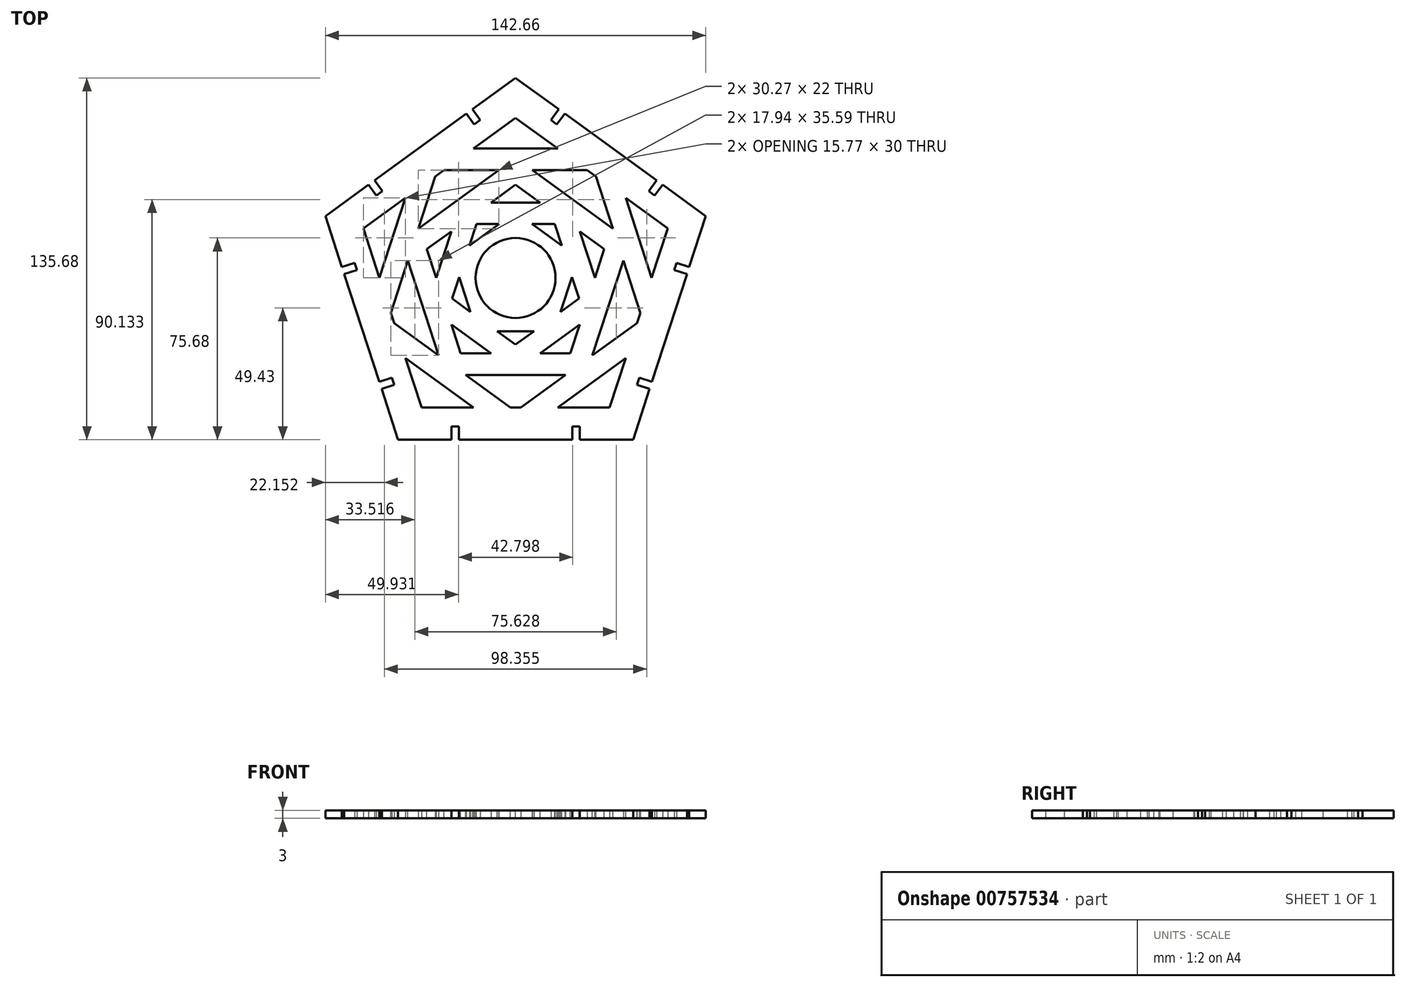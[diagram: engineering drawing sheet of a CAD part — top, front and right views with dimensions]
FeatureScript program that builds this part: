
annotation { "Feature Type Name" : "Feature", "Feature Type Description" : "" }
export const myFeature = defineFeature(function(context is Context, id is Id, definition is map)
    precondition{}
    {
        {
            var Q0;
            Q0=qCreatedBy(makeId("Top.planeOp"),FACE);
            var sketch = newSketch(context, id + "F0", { "sketchPlane" : qUnion([Q0])});
            skCircle(sketch, "E0.cCircle", {"center": v(0, 0) * mm, "radius": 75 * mm, "construction": true});
            skLineSegment(sketch, "E0.0", {"start": v(0, 75) * mm, "end": v(16.18, 63.24) * mm});
            skLineSegment(sketch, "E0.1", {"start": v(71.33, 23.18) * mm, "end": v(65.15, 4.16) * mm});
            skLineSegment(sketch, "E0.2", {"start": v(44.08, -60.68) * mm, "end": v(24.08, -60.68) * mm});
            skLineSegment(sketch, "E0.3", {"start": v(-44.08, -60.68) * mm, "end": v(-50.26, -41.66) * mm});
            skLineSegment(sketch, "E0.4", {"start": v(-71.33, 23.18) * mm, "end": v(-55.15, 34.93) * mm});
            skLineSegment(sketch, "E1", {"start": v(-16.18, 63.24) * mm, "end": v(-13.24, 59.2) * mm});
            skLineSegment(sketch, "E2", {"start": v(-13.24, 59.2) * mm, "end": v(-15.5, 57.55) * mm});
            skLineSegment(sketch, "E3", {"start": v(-15.5, 57.55) * mm, "end": v(-18.45, 61.6) * mm});
            skLineSegment(sketch, "E4", {"start": v(-35.66, 49.09) * mm, "end": v(44.08, -60.68) * mm, "construction": true});
            skLineSegment(sketch, "E5", {"start": v(-44.08, -60.68) * mm, "end": v(35.66, 49.09) * mm, "construction": true});
            skLineSegment(sketch, "E6", {"start": v(-71.33, 23.18) * mm, "end": v(57.7, -18.75) * mm, "construction": true});
            skLineSegment(sketch, "E7", {"start": v(71.33, 23.18) * mm, "end": v(-57.7, -18.75) * mm, "construction": true});
            skLineSegment(sketch, "E8", {"start": v(0, 75) * mm, "end": v(0, -60.68) * mm, "construction": true});
            skLineSegment(sketch, "E9.trimOffspring", {"start": v(-16.18, 63.24) * mm, "end": v(0, 75) * mm});
            skLineSegment(sketch, "E10.MirrorCS", {"start": v(-55.15, 34.93) * mm, "end": v(-52.2, 30.89) * mm});
            skLineSegment(sketch, "E11.MirrorCS", {"start": v(-49.94, 32.53) * mm, "end": v(-52.88, 36.58) * mm});
            skLineSegment(sketch, "E12.MirrorCS", {"start": v(-52.2, 30.89) * mm, "end": v(-49.94, 32.53) * mm});
            skLineSegment(sketch, "E13.trimOffspring", {"start": v(-52.88, 36.58) * mm, "end": v(-18.45, 61.6) * mm});
            skLineSegment(sketch, "E14.1.0", {"start": v(-65.15, 4.16) * mm, "end": v(-60.4, 5.7) * mm});
            skLineSegment(sketch, "E14.1.1", {"start": v(-59.53, 3.04) * mm, "end": v(-64.28, 1.5) * mm});
            skLineSegment(sketch, "E14.1.2", {"start": v(-60.4, 5.7) * mm, "end": v(-59.53, 3.04) * mm});
            skLineSegment(sketch, "E14.1.3", {"start": v(-46.37, -37.45) * mm, "end": v(-51.13, -39) * mm});
            skLineSegment(sketch, "E14.1.4", {"start": v(-45.5, -40.11) * mm, "end": v(-46.37, -37.45) * mm});
            skLineSegment(sketch, "E14.1.5", {"start": v(-50.26, -41.66) * mm, "end": v(-45.5, -40.11) * mm});
            skLineSegment(sketch, "E14.2.0", {"start": v(-24.08, -60.68) * mm, "end": v(-24.08, -55.68) * mm});
            skLineSegment(sketch, "E14.2.1", {"start": v(-21.28, -55.68) * mm, "end": v(-21.28, -60.68) * mm});
            skLineSegment(sketch, "E14.2.2", {"start": v(-24.08, -55.68) * mm, "end": v(-21.28, -55.68) * mm});
            skLineSegment(sketch, "E14.2.3", {"start": v(21.28, -55.68) * mm, "end": v(21.28, -60.68) * mm});
            skLineSegment(sketch, "E14.2.4", {"start": v(24.08, -55.68) * mm, "end": v(21.28, -55.68) * mm});
            skLineSegment(sketch, "E14.2.5", {"start": v(24.08, -60.68) * mm, "end": v(24.08, -55.68) * mm});
            skLineSegment(sketch, "E14.3.0", {"start": v(50.26, -41.66) * mm, "end": v(45.5, -40.11) * mm});
            skLineSegment(sketch, "E14.3.1", {"start": v(46.37, -37.45) * mm, "end": v(51.13, -39) * mm});
            skLineSegment(sketch, "E14.3.2", {"start": v(45.5, -40.11) * mm, "end": v(46.37, -37.45) * mm});
            skLineSegment(sketch, "E14.3.3", {"start": v(59.53, 3.04) * mm, "end": v(64.28, 1.5) * mm});
            skLineSegment(sketch, "E14.3.4", {"start": v(60.4, 5.7) * mm, "end": v(59.53, 3.04) * mm});
            skLineSegment(sketch, "E14.3.5", {"start": v(65.15, 4.16) * mm, "end": v(60.4, 5.7) * mm});
            skLineSegment(sketch, "E14.4.0", {"start": v(55.15, 34.93) * mm, "end": v(52.2, 30.89) * mm});
            skLineSegment(sketch, "E14.4.1", {"start": v(49.94, 32.53) * mm, "end": v(52.88, 36.58) * mm});
            skLineSegment(sketch, "E14.4.2", {"start": v(52.2, 30.89) * mm, "end": v(49.94, 32.53) * mm});
            skLineSegment(sketch, "E14.4.3", {"start": v(15.5, 57.55) * mm, "end": v(18.45, 61.6) * mm});
            skLineSegment(sketch, "E14.4.4", {"start": v(13.24, 59.2) * mm, "end": v(15.5, 57.55) * mm});
            skLineSegment(sketch, "E14.4.5", {"start": v(16.18, 63.24) * mm, "end": v(13.24, 59.2) * mm});
            skLineSegment(sketch, "E15.trimOffspring", {"start": v(-65.15, 4.16) * mm, "end": v(-71.33, 23.18) * mm});
            skLineSegment(sketch, "E16.trimOffspring", {"start": v(21.28, -60.68) * mm, "end": v(-21.28, -60.68) * mm});
            skLineSegment(sketch, "E17.trimOffspring", {"start": v(-24.08, -60.68) * mm, "end": v(-44.08, -60.68) * mm});
            skLineSegment(sketch, "E18.trimOffspring", {"start": v(-51.13, -39) * mm, "end": v(-64.28, 1.5) * mm});
            skLineSegment(sketch, "E19.trimOffspring", {"start": v(18.45, 61.6) * mm, "end": v(52.88, 36.58) * mm});
            skLineSegment(sketch, "E20.trimOffspring", {"start": v(55.15, 34.93) * mm, "end": v(71.33, 23.18) * mm});
            skLineSegment(sketch, "E21.trimOffspring", {"start": v(64.28, 1.5) * mm, "end": v(51.13, -39) * mm});
            skLineSegment(sketch, "E22.trimOffspring", {"start": v(50.26, -41.66) * mm, "end": v(44.08, -60.68) * mm});
            skCircle(sketch, "E23.cCircle", {"center": v(0, 0) * mm, "radius": 60 * mm, "construction": true});
            skLineSegment(sketch, "E23.0", {"start": v(0, 60) * mm, "end": v(57.06, 18.54) * mm});
            skLineSegment(sketch, "E23.1", {"start": v(57.06, 18.54) * mm, "end": v(35.27, -48.54) * mm});
            skLineSegment(sketch, "E23.2", {"start": v(35.27, -48.54) * mm, "end": v(-35.27, -48.54) * mm});
            skLineSegment(sketch, "E23.3", {"start": v(-35.27, -48.54) * mm, "end": v(-57.06, 18.54) * mm});
            skLineSegment(sketch, "E23.4", {"start": v(-57.06, 18.54) * mm, "end": v(0, 60) * mm});
            skSolve(sketch);
        }
        {
            var Q0;
            Q0 = qSketchRegion(id + "F0", true);
            extrude(context, id + "F1", {"entities" : qUnion([Q0]), "depth" : 3 * mm, "offsetDistance" : 25 * mm});
        }
        {
            var Q0;
            Q0=makeQuery(id+"F1.opExtrude","CAP_FACE",FACE,{"disambiguationData":[OSD([sQuery(id+"F0.wireOp",EDGE,"E0.0"),sQuery(id+"F0.wireOp",EDGE,"E0.1"),sQuery(id+"F0.wireOp",EDGE,"E0.2"),sQuery(id+"F0.wireOp",EDGE,"E0.3"),sQuery(id+"F0.wireOp",EDGE,"E0.4"),sQuery(id+"F0.wireOp",EDGE,"E1"),sQuery(id+"F0.wireOp",EDGE,"E2"),sQuery(id+"F0.wireOp",EDGE,"E3"),sQuery(id+"F0.wireOp",EDGE,"E9.trimOffspring"),sQuery(id+"F0.wireOp",EDGE,"E10.MirrorCS"),sQuery(id+"F0.wireOp",EDGE,"E11.MirrorCS"),sQuery(id+"F0.wireOp",EDGE,"E12.MirrorCS"),sQuery(id+"F0.wireOp",EDGE,"E13.trimOffspring"),sQuery(id+"F0.wireOp",EDGE,"E14.1.0"),sQuery(id+"F0.wireOp",EDGE,"E14.1.1"),sQuery(id+"F0.wireOp",EDGE,"E14.1.2"),sQuery(id+"F0.wireOp",EDGE,"E14.1.3"),sQuery(id+"F0.wireOp",EDGE,"E14.1.4"),sQuery(id+"F0.wireOp",EDGE,"E14.1.5"),sQuery(id+"F0.wireOp",EDGE,"E14.2.0"),sQuery(id+"F0.wireOp",EDGE,"E14.2.1"),sQuery(id+"F0.wireOp",EDGE,"E14.2.2"),sQuery(id+"F0.wireOp",EDGE,"E14.2.3"),sQuery(id+"F0.wireOp",EDGE,"E14.2.4"),sQuery(id+"F0.wireOp",EDGE,"E14.2.5"),sQuery(id+"F0.wireOp",EDGE,"E14.3.0"),sQuery(id+"F0.wireOp",EDGE,"E14.3.1"),sQuery(id+"F0.wireOp",EDGE,"E14.3.2"),sQuery(id+"F0.wireOp",EDGE,"E14.3.3"),sQuery(id+"F0.wireOp",EDGE,"E14.3.4"),sQuery(id+"F0.wireOp",EDGE,"E14.3.5"),sQuery(id+"F0.wireOp",EDGE,"E14.4.0"),sQuery(id+"F0.wireOp",EDGE,"E14.4.1"),sQuery(id+"F0.wireOp",EDGE,"E14.4.2"),sQuery(id+"F0.wireOp",EDGE,"E14.4.3"),sQuery(id+"F0.wireOp",EDGE,"E14.4.4"),sQuery(id+"F0.wireOp",EDGE,"E14.4.5"),sQuery(id+"F0.wireOp",EDGE,"E15.trimOffspring"),sQuery(id+"F0.wireOp",EDGE,"E16.trimOffspring"),sQuery(id+"F0.wireOp",EDGE,"E17.trimOffspring"),sQuery(id+"F0.wireOp",EDGE,"E18.trimOffspring"),sQuery(id+"F0.wireOp",EDGE,"E19.trimOffspring"),sQuery(id+"F0.wireOp",EDGE,"E20.trimOffspring"),sQuery(id+"F0.wireOp",EDGE,"E21.trimOffspring"),sQuery(id+"F0.wireOp",EDGE,"E22.trimOffspring"),sQuery(id+"F0.wireOp",EDGE,"E23.0"),sQuery(id+"F0.wireOp",EDGE,"E23.1"),sQuery(id+"F0.wireOp",EDGE,"E23.2"),sQuery(id+"F0.wireOp",EDGE,"E23.3"),sQuery(id+"F0.wireOp",EDGE,"E23.4")])],"isStart":false});
            var sketch = newSketch(context, id + "F2", { "sketchPlane" : qUnion([Q0])});
            skCircle(sketch, "E24.cCircle", {"center": v(0, 0) * mm, "radius": 60 * mm, "construction": true});
            skLineSegment(sketch, "E24.0", {"start": v(0, -60) * mm, "end": v(-57.06, -18.54) * mm});
            skLineSegment(sketch, "E24.1", {"start": v(-57.06, -18.54) * mm, "end": v(-35.27, 48.54) * mm});
            skLineSegment(sketch, "E24.2", {"start": v(-35.27, 48.54) * mm, "end": v(35.27, 48.54) * mm});
            skLineSegment(sketch, "E24.3", {"start": v(35.27, 48.54) * mm, "end": v(57.06, -18.54) * mm});
            skLineSegment(sketch, "E24.4", {"start": v(57.06, -18.54) * mm, "end": v(0, -60) * mm});
            skCircle(sketch, "E25.cCircle", {"center": v(0, 0) * mm, "radius": 50 * mm, "construction": true});
            skLineSegment(sketch, "E25.0", {"start": v(0, -50) * mm, "end": v(-47.55, -15.45) * mm});
            skLineSegment(sketch, "E25.1", {"start": v(-47.55, -15.45) * mm, "end": v(-29.39, 40.45) * mm});
            skLineSegment(sketch, "E25.2", {"start": v(-29.39, 40.45) * mm, "end": v(29.39, 40.45) * mm});
            skLineSegment(sketch, "E25.3", {"start": v(29.39, 40.45) * mm, "end": v(47.55, -15.45) * mm});
            skLineSegment(sketch, "E25.4", {"start": v(47.55, -15.45) * mm, "end": v(0, -50) * mm});
            skSolve(sketch);
        }
        {
            var Q0;
            Q0 = qSketchRegion(id + "F2", true);
            extrude(context, id + "F3", {"entities" : qUnion([Q0]), "operationType" : NewBodyOperationType.ADD, "oppositeDirection" : true, "depth" : 3 * mm, "offsetDistance" : 25 * mm});
        }
        {
            var Q0;
            Q0=makeQuery(id+"F3.boolean.opBoolean","MERGE",FACE,{"derivedFrom":[makeQuery(id+"F1.opExtrude","CAP_FACE",FACE,{"disambiguationData":[OSD([sQuery(id+"F0.wireOp",EDGE,"E0.0"),sQuery(id+"F0.wireOp",EDGE,"E0.1"),sQuery(id+"F0.wireOp",EDGE,"E0.2"),sQuery(id+"F0.wireOp",EDGE,"E0.3"),sQuery(id+"F0.wireOp",EDGE,"E0.4"),sQuery(id+"F0.wireOp",EDGE,"E1"),sQuery(id+"F0.wireOp",EDGE,"E2"),sQuery(id+"F0.wireOp",EDGE,"E3"),sQuery(id+"F0.wireOp",EDGE,"E9.trimOffspring"),sQuery(id+"F0.wireOp",EDGE,"E10.MirrorCS"),sQuery(id+"F0.wireOp",EDGE,"E11.MirrorCS"),sQuery(id+"F0.wireOp",EDGE,"E12.MirrorCS"),sQuery(id+"F0.wireOp",EDGE,"E13.trimOffspring"),sQuery(id+"F0.wireOp",EDGE,"E14.1.0"),sQuery(id+"F0.wireOp",EDGE,"E14.1.1"),sQuery(id+"F0.wireOp",EDGE,"E14.1.2"),sQuery(id+"F0.wireOp",EDGE,"E14.1.3"),sQuery(id+"F0.wireOp",EDGE,"E14.1.4"),sQuery(id+"F0.wireOp",EDGE,"E14.1.5"),sQuery(id+"F0.wireOp",EDGE,"E14.2.0"),sQuery(id+"F0.wireOp",EDGE,"E14.2.1"),sQuery(id+"F0.wireOp",EDGE,"E14.2.2"),sQuery(id+"F0.wireOp",EDGE,"E14.2.3"),sQuery(id+"F0.wireOp",EDGE,"E14.2.4"),sQuery(id+"F0.wireOp",EDGE,"E14.2.5"),sQuery(id+"F0.wireOp",EDGE,"E14.3.0"),sQuery(id+"F0.wireOp",EDGE,"E14.3.1"),sQuery(id+"F0.wireOp",EDGE,"E14.3.2"),sQuery(id+"F0.wireOp",EDGE,"E14.3.3"),sQuery(id+"F0.wireOp",EDGE,"E14.3.4"),sQuery(id+"F0.wireOp",EDGE,"E14.3.5"),sQuery(id+"F0.wireOp",EDGE,"E14.4.0"),sQuery(id+"F0.wireOp",EDGE,"E14.4.1"),sQuery(id+"F0.wireOp",EDGE,"E14.4.2"),sQuery(id+"F0.wireOp",EDGE,"E14.4.3"),sQuery(id+"F0.wireOp",EDGE,"E14.4.4"),sQuery(id+"F0.wireOp",EDGE,"E14.4.5"),sQuery(id+"F0.wireOp",EDGE,"E15.trimOffspring"),sQuery(id+"F0.wireOp",EDGE,"E16.trimOffspring"),sQuery(id+"F0.wireOp",EDGE,"E17.trimOffspring"),sQuery(id+"F0.wireOp",EDGE,"E18.trimOffspring"),sQuery(id+"F0.wireOp",EDGE,"E19.trimOffspring"),sQuery(id+"F0.wireOp",EDGE,"E20.trimOffspring"),sQuery(id+"F0.wireOp",EDGE,"E21.trimOffspring"),sQuery(id+"F0.wireOp",EDGE,"E22.trimOffspring"),sQuery(id+"F0.wireOp",EDGE,"E23.0"),sQuery(id+"F0.wireOp",EDGE,"E23.1"),sQuery(id+"F0.wireOp",EDGE,"E23.2"),sQuery(id+"F0.wireOp",EDGE,"E23.3"),sQuery(id+"F0.wireOp",EDGE,"E23.4")])],"isStart":false}),makeQuery(id+"F3.opExtrude","CAP_FACE",FACE,{"disambiguationData":[OSD([sQuery(id+"F2.wireOp",EDGE,"E24.0"),sQuery(id+"F2.wireOp",EDGE,"E24.1"),sQuery(id+"F2.wireOp",EDGE,"E24.2"),sQuery(id+"F2.wireOp",EDGE,"E24.3"),sQuery(id+"F2.wireOp",EDGE,"E24.4"),sQuery(id+"F2.wireOp",EDGE,"E25.0"),sQuery(id+"F2.wireOp",EDGE,"E25.1"),sQuery(id+"F2.wireOp",EDGE,"E25.2"),sQuery(id+"F2.wireOp",EDGE,"E25.3"),sQuery(id+"F2.wireOp",EDGE,"E25.4")])],"isStart":true})]});
            var sketch = newSketch(context, id + "F4", { "sketchPlane" : qUnion([Q0])});
            skCircle(sketch, "E26.cCircle", {"center": v(0, 0) * mm, "radius": 45 * mm, "construction": true});
            skLineSegment(sketch, "E26.0", {"start": v(0, 45) * mm, "end": v(42.8, 13.9) * mm});
            skLineSegment(sketch, "E26.1", {"start": v(42.8, 13.9) * mm, "end": v(26.45, -36.4) * mm});
            skLineSegment(sketch, "E26.2", {"start": v(26.45, -36.4) * mm, "end": v(-26.45, -36.4) * mm});
            skLineSegment(sketch, "E26.3", {"start": v(-26.45, -36.4) * mm, "end": v(-42.8, 13.9) * mm});
            skLineSegment(sketch, "E26.4", {"start": v(-42.8, 13.9) * mm, "end": v(0, 45) * mm});
            skCircle(sketch, "E27.cCircle", {"center": v(0, 0) * mm, "radius": 35 * mm, "construction": true});
            skLineSegment(sketch, "E27.0", {"start": v(0, 35) * mm, "end": v(33.29, 10.82) * mm});
            skLineSegment(sketch, "E27.1", {"start": v(33.29, 10.82) * mm, "end": v(20.57, -28.32) * mm});
            skLineSegment(sketch, "E27.2", {"start": v(20.57, -28.32) * mm, "end": v(-20.57, -28.32) * mm});
            skLineSegment(sketch, "E27.3", {"start": v(-20.57, -28.32) * mm, "end": v(-33.29, 10.82) * mm});
            skLineSegment(sketch, "E27.4", {"start": v(-33.29, 10.82) * mm, "end": v(0, 35) * mm});
            skSolve(sketch);
        }
        {
            var Q0;
            Q0 = qSketchRegion(id + "F4", true);
            extrude(context, id + "F5", {"entities" : qUnion([Q0]), "operationType" : NewBodyOperationType.ADD, "oppositeDirection" : true, "depth" : 3 * mm, "offsetDistance" : 25 * mm});
        }
        {
            var Q0;
            Q0=makeQuery(id+"F5.boolean.opBoolean","MERGE",FACE,{"derivedFrom":[makeQuery(id+"F3.boolean.opBoolean","MERGE",FACE,{"derivedFrom":[makeQuery(id+"F1.opExtrude","CAP_FACE",FACE,{"disambiguationData":[OSD([sQuery(id+"F0.wireOp",EDGE,"E0.0"),sQuery(id+"F0.wireOp",EDGE,"E0.1"),sQuery(id+"F0.wireOp",EDGE,"E0.2"),sQuery(id+"F0.wireOp",EDGE,"E0.3"),sQuery(id+"F0.wireOp",EDGE,"E0.4"),sQuery(id+"F0.wireOp",EDGE,"E1"),sQuery(id+"F0.wireOp",EDGE,"E2"),sQuery(id+"F0.wireOp",EDGE,"E3"),sQuery(id+"F0.wireOp",EDGE,"E9.trimOffspring"),sQuery(id+"F0.wireOp",EDGE,"E10.MirrorCS"),sQuery(id+"F0.wireOp",EDGE,"E11.MirrorCS"),sQuery(id+"F0.wireOp",EDGE,"E12.MirrorCS"),sQuery(id+"F0.wireOp",EDGE,"E13.trimOffspring"),sQuery(id+"F0.wireOp",EDGE,"E14.1.0"),sQuery(id+"F0.wireOp",EDGE,"E14.1.1"),sQuery(id+"F0.wireOp",EDGE,"E14.1.2"),sQuery(id+"F0.wireOp",EDGE,"E14.1.3"),sQuery(id+"F0.wireOp",EDGE,"E14.1.4"),sQuery(id+"F0.wireOp",EDGE,"E14.1.5"),sQuery(id+"F0.wireOp",EDGE,"E14.2.0"),sQuery(id+"F0.wireOp",EDGE,"E14.2.1"),sQuery(id+"F0.wireOp",EDGE,"E14.2.2"),sQuery(id+"F0.wireOp",EDGE,"E14.2.3"),sQuery(id+"F0.wireOp",EDGE,"E14.2.4"),sQuery(id+"F0.wireOp",EDGE,"E14.2.5"),sQuery(id+"F0.wireOp",EDGE,"E14.3.0"),sQuery(id+"F0.wireOp",EDGE,"E14.3.1"),sQuery(id+"F0.wireOp",EDGE,"E14.3.2"),sQuery(id+"F0.wireOp",EDGE,"E14.3.3"),sQuery(id+"F0.wireOp",EDGE,"E14.3.4"),sQuery(id+"F0.wireOp",EDGE,"E14.3.5"),sQuery(id+"F0.wireOp",EDGE,"E14.4.0"),sQuery(id+"F0.wireOp",EDGE,"E14.4.1"),sQuery(id+"F0.wireOp",EDGE,"E14.4.2"),sQuery(id+"F0.wireOp",EDGE,"E14.4.3"),sQuery(id+"F0.wireOp",EDGE,"E14.4.4"),sQuery(id+"F0.wireOp",EDGE,"E14.4.5"),sQuery(id+"F0.wireOp",EDGE,"E15.trimOffspring"),sQuery(id+"F0.wireOp",EDGE,"E16.trimOffspring"),sQuery(id+"F0.wireOp",EDGE,"E17.trimOffspring"),sQuery(id+"F0.wireOp",EDGE,"E18.trimOffspring"),sQuery(id+"F0.wireOp",EDGE,"E19.trimOffspring"),sQuery(id+"F0.wireOp",EDGE,"E20.trimOffspring"),sQuery(id+"F0.wireOp",EDGE,"E21.trimOffspring"),sQuery(id+"F0.wireOp",EDGE,"E22.trimOffspring"),sQuery(id+"F0.wireOp",EDGE,"E23.0"),sQuery(id+"F0.wireOp",EDGE,"E23.1"),sQuery(id+"F0.wireOp",EDGE,"E23.2"),sQuery(id+"F0.wireOp",EDGE,"E23.3"),sQuery(id+"F0.wireOp",EDGE,"E23.4")])],"isStart":false}),makeQuery(id+"F3.opExtrude","CAP_FACE",FACE,{"disambiguationData":[OSD([sQuery(id+"F2.wireOp",EDGE,"E24.0"),sQuery(id+"F2.wireOp",EDGE,"E24.1"),sQuery(id+"F2.wireOp",EDGE,"E24.2"),sQuery(id+"F2.wireOp",EDGE,"E24.3"),sQuery(id+"F2.wireOp",EDGE,"E24.4"),sQuery(id+"F2.wireOp",EDGE,"E25.0"),sQuery(id+"F2.wireOp",EDGE,"E25.1"),sQuery(id+"F2.wireOp",EDGE,"E25.2"),sQuery(id+"F2.wireOp",EDGE,"E25.3"),sQuery(id+"F2.wireOp",EDGE,"E25.4")])],"isStart":true})]}),makeQuery(id+"F5.opExtrude","CAP_FACE",FACE,{"disambiguationData":[OSD([sQuery(id+"F4.wireOp",EDGE,"E26.0"),sQuery(id+"F4.wireOp",EDGE,"E26.1"),sQuery(id+"F4.wireOp",EDGE,"E26.2"),sQuery(id+"F4.wireOp",EDGE,"E26.3"),sQuery(id+"F4.wireOp",EDGE,"E26.4"),sQuery(id+"F4.wireOp",EDGE,"E27.0"),sQuery(id+"F4.wireOp",EDGE,"E27.1"),sQuery(id+"F4.wireOp",EDGE,"E27.2"),sQuery(id+"F4.wireOp",EDGE,"E27.3"),sQuery(id+"F4.wireOp",EDGE,"E27.4")])],"isStart":true})]});
            var sketch = newSketch(context, id + "F6", { "sketchPlane" : qUnion([Q0])});
            skCircle(sketch, "E28.cCircle", {"center": v(0, 0) * mm, "radius": 25 * mm, "construction": true});
            skLineSegment(sketch, "E28.0", {"start": v(0, -25) * mm, "end": v(-23.78, -7.73) * mm});
            skLineSegment(sketch, "E28.1", {"start": v(-23.78, -7.73) * mm, "end": v(-14.7, 20.23) * mm});
            skLineSegment(sketch, "E28.2", {"start": v(-14.7, 20.23) * mm, "end": v(14.7, 20.23) * mm});
            skLineSegment(sketch, "E28.3", {"start": v(14.7, 20.23) * mm, "end": v(23.78, -7.73) * mm});
            skLineSegment(sketch, "E28.4", {"start": v(23.78, -7.73) * mm, "end": v(0, -25) * mm});
            skCircle(sketch, "E29.cCircle", {"center": v(0, 0) * mm, "radius": 35 * mm, "construction": true});
            skLineSegment(sketch, "E29.0", {"start": v(0, -35) * mm, "end": v(-33.29, -10.82) * mm});
            skLineSegment(sketch, "E29.1", {"start": v(-33.29, -10.82) * mm, "end": v(-20.57, 28.32) * mm});
            skLineSegment(sketch, "E29.2", {"start": v(-20.57, 28.32) * mm, "end": v(20.57, 28.32) * mm});
            skLineSegment(sketch, "E29.3", {"start": v(20.57, 28.32) * mm, "end": v(33.29, -10.82) * mm});
            skLineSegment(sketch, "E29.4", {"start": v(33.29, -10.82) * mm, "end": v(0, -35) * mm});
            skSolve(sketch);
        }
        {
            var Q0;
            Q0 = qSketchRegion(id + "F6", true);
            extrude(context, id + "F7", {"entities" : qUnion([Q0]), "operationType" : NewBodyOperationType.ADD, "oppositeDirection" : true, "depth" : 3 * mm, "offsetDistance" : 25 * mm});
        }
        {
            var Q0;
            Q0=makeQuery(id+"F7.boolean.opBoolean","MERGE",FACE,{"derivedFrom":[makeQuery(id+"F5.boolean.opBoolean","MERGE",FACE,{"derivedFrom":[makeQuery(id+"F3.boolean.opBoolean","MERGE",FACE,{"derivedFrom":[makeQuery(id+"F1.opExtrude","CAP_FACE",FACE,{"disambiguationData":[OSD([sQuery(id+"F0.wireOp",EDGE,"E0.0"),sQuery(id+"F0.wireOp",EDGE,"E0.1"),sQuery(id+"F0.wireOp",EDGE,"E0.2"),sQuery(id+"F0.wireOp",EDGE,"E0.3"),sQuery(id+"F0.wireOp",EDGE,"E0.4"),sQuery(id+"F0.wireOp",EDGE,"E1"),sQuery(id+"F0.wireOp",EDGE,"E2"),sQuery(id+"F0.wireOp",EDGE,"E3"),sQuery(id+"F0.wireOp",EDGE,"E9.trimOffspring"),sQuery(id+"F0.wireOp",EDGE,"E10.MirrorCS"),sQuery(id+"F0.wireOp",EDGE,"E11.MirrorCS"),sQuery(id+"F0.wireOp",EDGE,"E12.MirrorCS"),sQuery(id+"F0.wireOp",EDGE,"E13.trimOffspring"),sQuery(id+"F0.wireOp",EDGE,"E14.1.0"),sQuery(id+"F0.wireOp",EDGE,"E14.1.1"),sQuery(id+"F0.wireOp",EDGE,"E14.1.2"),sQuery(id+"F0.wireOp",EDGE,"E14.1.3"),sQuery(id+"F0.wireOp",EDGE,"E14.1.4"),sQuery(id+"F0.wireOp",EDGE,"E14.1.5"),sQuery(id+"F0.wireOp",EDGE,"E14.2.0"),sQuery(id+"F0.wireOp",EDGE,"E14.2.1"),sQuery(id+"F0.wireOp",EDGE,"E14.2.2"),sQuery(id+"F0.wireOp",EDGE,"E14.2.3"),sQuery(id+"F0.wireOp",EDGE,"E14.2.4"),sQuery(id+"F0.wireOp",EDGE,"E14.2.5"),sQuery(id+"F0.wireOp",EDGE,"E14.3.0"),sQuery(id+"F0.wireOp",EDGE,"E14.3.1"),sQuery(id+"F0.wireOp",EDGE,"E14.3.2"),sQuery(id+"F0.wireOp",EDGE,"E14.3.3"),sQuery(id+"F0.wireOp",EDGE,"E14.3.4"),sQuery(id+"F0.wireOp",EDGE,"E14.3.5"),sQuery(id+"F0.wireOp",EDGE,"E14.4.0"),sQuery(id+"F0.wireOp",EDGE,"E14.4.1"),sQuery(id+"F0.wireOp",EDGE,"E14.4.2"),sQuery(id+"F0.wireOp",EDGE,"E14.4.3"),sQuery(id+"F0.wireOp",EDGE,"E14.4.4"),sQuery(id+"F0.wireOp",EDGE,"E14.4.5"),sQuery(id+"F0.wireOp",EDGE,"E15.trimOffspring"),sQuery(id+"F0.wireOp",EDGE,"E16.trimOffspring"),sQuery(id+"F0.wireOp",EDGE,"E17.trimOffspring"),sQuery(id+"F0.wireOp",EDGE,"E18.trimOffspring"),sQuery(id+"F0.wireOp",EDGE,"E19.trimOffspring"),sQuery(id+"F0.wireOp",EDGE,"E20.trimOffspring"),sQuery(id+"F0.wireOp",EDGE,"E21.trimOffspring"),sQuery(id+"F0.wireOp",EDGE,"E22.trimOffspring"),sQuery(id+"F0.wireOp",EDGE,"E23.0"),sQuery(id+"F0.wireOp",EDGE,"E23.1"),sQuery(id+"F0.wireOp",EDGE,"E23.2"),sQuery(id+"F0.wireOp",EDGE,"E23.3"),sQuery(id+"F0.wireOp",EDGE,"E23.4")])],"isStart":false}),makeQuery(id+"F3.opExtrude","CAP_FACE",FACE,{"disambiguationData":[OSD([sQuery(id+"F2.wireOp",EDGE,"E24.0"),sQuery(id+"F2.wireOp",EDGE,"E24.1"),sQuery(id+"F2.wireOp",EDGE,"E24.2"),sQuery(id+"F2.wireOp",EDGE,"E24.3"),sQuery(id+"F2.wireOp",EDGE,"E24.4"),sQuery(id+"F2.wireOp",EDGE,"E25.0"),sQuery(id+"F2.wireOp",EDGE,"E25.1"),sQuery(id+"F2.wireOp",EDGE,"E25.2"),sQuery(id+"F2.wireOp",EDGE,"E25.3"),sQuery(id+"F2.wireOp",EDGE,"E25.4")])],"isStart":true})]}),makeQuery(id+"F5.opExtrude","CAP_FACE",FACE,{"disambiguationData":[OSD([sQuery(id+"F4.wireOp",EDGE,"E26.0"),sQuery(id+"F4.wireOp",EDGE,"E26.1"),sQuery(id+"F4.wireOp",EDGE,"E26.2"),sQuery(id+"F4.wireOp",EDGE,"E26.3"),sQuery(id+"F4.wireOp",EDGE,"E26.4"),sQuery(id+"F4.wireOp",EDGE,"E27.0"),sQuery(id+"F4.wireOp",EDGE,"E27.1"),sQuery(id+"F4.wireOp",EDGE,"E27.2"),sQuery(id+"F4.wireOp",EDGE,"E27.3"),sQuery(id+"F4.wireOp",EDGE,"E27.4")])],"isStart":true})]}),makeQuery(id+"F7.opExtrude","CAP_FACE",FACE,{"disambiguationData":[OSD([sQuery(id+"F6.wireOp",EDGE,"E28.0"),sQuery(id+"F6.wireOp",EDGE,"E28.1"),sQuery(id+"F6.wireOp",EDGE,"E28.2"),sQuery(id+"F6.wireOp",EDGE,"E28.3"),sQuery(id+"F6.wireOp",EDGE,"E28.4"),sQuery(id+"F6.wireOp",EDGE,"E29.0"),sQuery(id+"F6.wireOp",EDGE,"E29.1"),sQuery(id+"F6.wireOp",EDGE,"E29.2"),sQuery(id+"F6.wireOp",EDGE,"E29.3"),sQuery(id+"F6.wireOp",EDGE,"E29.4")])],"isStart":true})]});
            var sketch = newSketch(context, id + "F8", { "sketchPlane" : qUnion([Q0])});
            skCircle(sketch, "E30.cCircle", {"center": v(0, 0) * mm, "radius": 20 * mm, "construction": true});
            skLineSegment(sketch, "E30.0", {"start": v(14.53, -20) * mm, "end": v(-14.53, -20) * mm});
            skLineSegment(sketch, "E30.1", {"start": v(-14.53, -20) * mm, "end": v(-23.51, 7.64) * mm});
            skLineSegment(sketch, "E30.2", {"start": v(-23.51, 7.64) * mm, "end": v(0, 24.72) * mm});
            skLineSegment(sketch, "E30.3", {"start": v(0, 24.72) * mm, "end": v(23.51, 7.64) * mm});
            skLineSegment(sketch, "E30.4", {"start": v(23.51, 7.64) * mm, "end": v(14.53, -20) * mm});
            skPoint(sketch, "E30.0.midPoint", {"position": v(0, -20) * mm});
            skCircle(sketch, "E31", {"center": v(0, 0) * mm, "radius": 15 * mm});
            skSolve(sketch);
        }
        {
            var Q0;
            Q0 = qSketchRegion(id + "F8", true);
            extrude(context, id + "F9", {"entities" : qUnion([Q0]), "operationType" : NewBodyOperationType.ADD, "oppositeDirection" : true, "depth" : 3 * mm, "offsetDistance" : 25 * mm});
        }
    });
